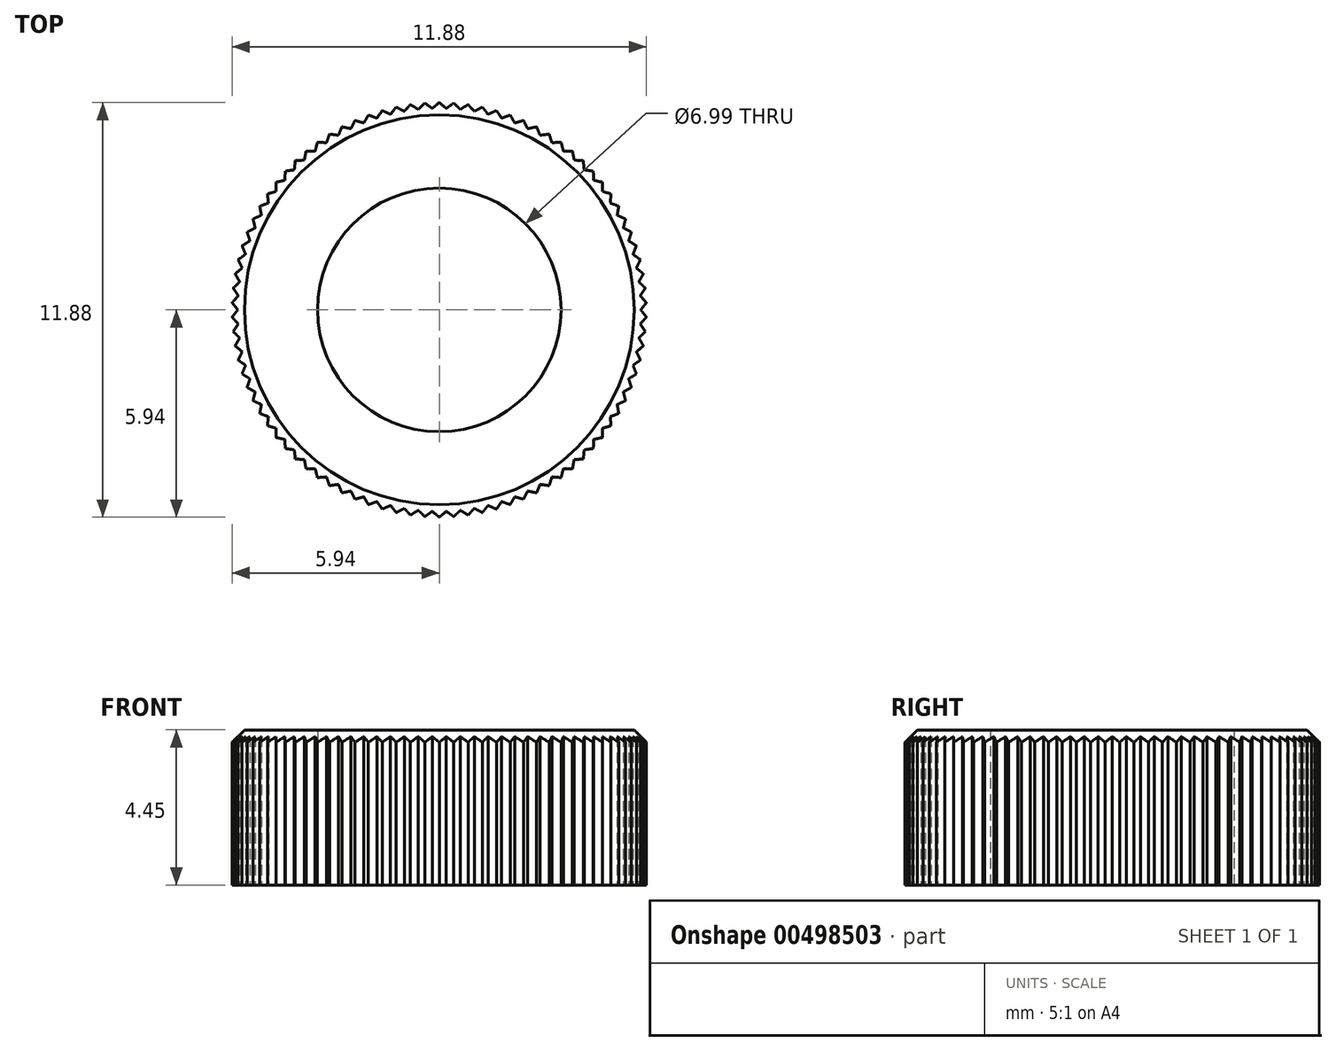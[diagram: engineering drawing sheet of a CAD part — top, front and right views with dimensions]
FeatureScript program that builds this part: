
annotation { "Feature Type Name" : "Feature", "Feature Type Description" : "" }
export const myFeature = defineFeature(function(context is Context, id is Id, definition is map)
    precondition{}
    {
        {
            var Q0;
            Q0=qCreatedBy(makeId("Front.planeOp"),FACE);
            var sketch = newSketch(context, id + "F0", { "sketchPlane" : qUnion([Q0])});
            skLineSegment(sketch, "E0", {"start": v(0, 0) * mm, "end": v(0, 10.81) * mm, "construction": true});
            skLineSegment(sketch, "E1", {"start": v(5.97, 0) * mm, "end": v(5.97, 4.45) * mm});
            skLineSegment(sketch, "E2", {"start": v(5.97, 4.45) * mm, "end": v(3.5, 4.45) * mm});
            skLineSegment(sketch, "E3", {"start": v(3.5, 4.45) * mm, "end": v(3.5, 0) * mm});
            skLineSegment(sketch, "E4", {"start": v(3.5, 0) * mm, "end": v(5.97, 0) * mm});
            skSolve(sketch);
        }
        {
            var Q0;
            Q0 = qSketchRegion(id + "F0", true);
            var Q1;
            Q1=sQuery(id+"F0.wireOp",EDGE,"E0");
            revolve(context, id + "F1", {"entities" : qUnion([Q0]), "axis" : qUnion([Q1]), "revolveType" : RevolveType.FULL});
        }
        {
            var Q0;
            Q0=makeQuery(id+"F1.opRevolve","SWEPT_EDGE",EDGE,{"disambiguationData":[OSD([sQuery(id+"F0.wireOp",EDGE,"E1"),sQuery(id+"F0.wireOp",EDGE,"E2")])]});
            chamfer(context, id + "F2", {"entities" : qUnion([Q0]), "width" : 0.38 * mm, "tangentPropagation" : true});
        }
        {
            var Q0;
            Q0=makeQuery(id+"F1.opRevolve","SWEPT_FACE",FACE,{"disambiguationData":[OSD([sQuery(id+"F0.wireOp",EDGE,"E4")])]});
            var sketch = newSketch(context, id + "F3", { "sketchPlane" : qUnion([Q0])});
            skLineSegment(sketch, "E5", {"start": v(0, 5.97) * mm, "end": v(0, 0) * mm, "construction": true});
            skPoint(sketch, "E6.orphan", {"position": v(0, 7.48) * mm});
            skCircle(sketch, "E7", {"center": v(0, 0) * mm, "radius": 5.78 * mm, "construction": true});
            skLineSegment(sketch, "E8", {"start": v(-0.2, 5.77) * mm, "end": v(0, 0) * mm, "construction": true});
            skLineSegment(sketch, "E9", {"start": v(0, 5.94) * mm, "end": v(-0.2, 5.77) * mm});
            skLineSegment(sketch, "E10.MirrorCS", {"start": v(0, 5.94) * mm, "end": v(0.2, 5.77) * mm});
            skLineSegment(sketch, "E11.1.0", {"start": v(-0.41, 5.93) * mm, "end": v(-0.2, 5.77) * mm});
            skLineSegment(sketch, "E11.1.1", {"start": v(-0.41, 5.93) * mm, "end": v(-0.6, 5.75) * mm});
            skLineSegment(sketch, "E11.2.0", {"start": v(-0.83, 5.89) * mm, "end": v(-0.6, 5.75) * mm});
            skLineSegment(sketch, "E11.2.1", {"start": v(-0.83, 5.89) * mm, "end": v(-1, 5.7) * mm});
            skLineSegment(sketch, "E11.3.0", {"start": v(-1.24, 5.81) * mm, "end": v(-1, 5.7) * mm});
            skLineSegment(sketch, "E11.3.1", {"start": v(-1.24, 5.81) * mm, "end": v(-1.4, 5.6) * mm});
            skLineSegment(sketch, "E11.4.0", {"start": v(-1.64, 5.71) * mm, "end": v(-1.4, 5.6) * mm});
            skLineSegment(sketch, "E11.4.1", {"start": v(-1.64, 5.71) * mm, "end": v(-1.79, 5.5) * mm});
            skLineSegment(sketch, "E11.5.0", {"start": v(-2.03, 5.59) * mm, "end": v(-1.79, 5.5) * mm});
            skLineSegment(sketch, "E11.5.1", {"start": v(-2.03, 5.59) * mm, "end": v(-2.16, 5.36) * mm});
            skLineSegment(sketch, "E11.6.0", {"start": v(-2.42, 5.43) * mm, "end": v(-2.16, 5.36) * mm});
            skLineSegment(sketch, "E11.6.1", {"start": v(-2.42, 5.43) * mm, "end": v(-2.53, 5.2) * mm});
            skLineSegment(sketch, "E11.7.0", {"start": v(-2.8, 5.25) * mm, "end": v(-2.53, 5.2) * mm});
            skLineSegment(sketch, "E11.7.1", {"start": v(-2.8, 5.25) * mm, "end": v(-2.89, 5) * mm});
            skLineSegment(sketch, "E11.8.0", {"start": v(-3.15, 5.04) * mm, "end": v(-2.89, 5) * mm});
            skLineSegment(sketch, "E11.8.1", {"start": v(-3.15, 5.04) * mm, "end": v(-3.23, 4.8) * mm});
            skLineSegment(sketch, "E11.9.0", {"start": v(-3.5, 4.8) * mm, "end": v(-3.23, 4.8) * mm});
            skLineSegment(sketch, "E11.9.1", {"start": v(-3.5, 4.8) * mm, "end": v(-3.56, 4.55) * mm});
            skLineSegment(sketch, "E11.10.0", {"start": v(-3.82, 4.55) * mm, "end": v(-3.56, 4.55) * mm});
            skLineSegment(sketch, "E11.10.1", {"start": v(-3.82, 4.55) * mm, "end": v(-3.87, 4.3) * mm});
            skLineSegment(sketch, "E11.11.0", {"start": v(-4.13, 4.28) * mm, "end": v(-3.87, 4.3) * mm});
            skLineSegment(sketch, "E11.11.1", {"start": v(-4.13, 4.28) * mm, "end": v(-4.16, 4.01) * mm});
            skLineSegment(sketch, "E11.12.0", {"start": v(-4.42, 3.98) * mm, "end": v(-4.16, 4.01) * mm});
            skLineSegment(sketch, "E11.12.1", {"start": v(-4.42, 3.98) * mm, "end": v(-4.43, 3.71) * mm});
            skLineSegment(sketch, "E11.13.0", {"start": v(-4.68, 3.66) * mm, "end": v(-4.43, 3.71) * mm});
            skLineSegment(sketch, "E11.13.1", {"start": v(-4.68, 3.66) * mm, "end": v(-4.67, 3.4) * mm});
            skLineSegment(sketch, "E11.14.0", {"start": v(-4.93, 3.32) * mm, "end": v(-4.67, 3.4) * mm});
            skLineSegment(sketch, "E11.14.1", {"start": v(-4.93, 3.32) * mm, "end": v(-4.9, 3.06) * mm});
            skLineSegment(sketch, "E11.15.0", {"start": v(-5.15, 2.97) * mm, "end": v(-4.9, 3.06) * mm});
            skLineSegment(sketch, "E11.15.1", {"start": v(-5.15, 2.97) * mm, "end": v(-5.1, 2.71) * mm});
            skLineSegment(sketch, "E11.16.0", {"start": v(-5.34, 2.6) * mm, "end": v(-5.1, 2.71) * mm});
            skLineSegment(sketch, "E11.16.1", {"start": v(-5.34, 2.6) * mm, "end": v(-5.28, 2.35) * mm});
            skLineSegment(sketch, "E11.17.0", {"start": v(-5.51, 2.23) * mm, "end": v(-5.28, 2.35) * mm});
            skLineSegment(sketch, "E11.17.1", {"start": v(-5.51, 2.23) * mm, "end": v(-5.43, 1.98) * mm});
            skLineSegment(sketch, "E11.18.0", {"start": v(-5.65, 1.84) * mm, "end": v(-5.43, 1.98) * mm});
            skLineSegment(sketch, "E11.18.1", {"start": v(-5.65, 1.84) * mm, "end": v(-5.55, 1.6) * mm});
            skLineSegment(sketch, "E11.19.0", {"start": v(-5.77, 1.44) * mm, "end": v(-5.55, 1.6) * mm});
            skLineSegment(sketch, "E11.19.1", {"start": v(-5.77, 1.44) * mm, "end": v(-5.65, 1.2) * mm});
            skLineSegment(sketch, "E11.20.0", {"start": v(-5.85, 1.03) * mm, "end": v(-5.65, 1.2) * mm});
            skLineSegment(sketch, "E11.20.1", {"start": v(-5.85, 1.03) * mm, "end": v(-5.72, 0.8) * mm});
            skLineSegment(sketch, "E11.21.0", {"start": v(-5.91, 0.62) * mm, "end": v(-5.72, 0.8) * mm});
            skLineSegment(sketch, "E11.21.1", {"start": v(-5.91, 0.62) * mm, "end": v(-5.76, 0.4) * mm});
            skLineSegment(sketch, "E11.22.0", {"start": v(-5.94, 0.2) * mm, "end": v(-5.76, 0.4) * mm});
            skLineSegment(sketch, "E11.22.1", {"start": v(-5.94, 0.2) * mm, "end": v(-5.78, 0) * mm});
            skLineSegment(sketch, "E11.23.0", {"start": v(-5.94, -0.2) * mm, "end": v(-5.78, 0) * mm});
            skLineSegment(sketch, "E11.23.1", {"start": v(-5.94, -0.2) * mm, "end": v(-5.76, -0.4) * mm});
            skLineSegment(sketch, "E11.24.0", {"start": v(-5.91, -0.62) * mm, "end": v(-5.76, -0.4) * mm});
            skLineSegment(sketch, "E11.24.1", {"start": v(-5.91, -0.62) * mm, "end": v(-5.72, -0.8) * mm});
            skLineSegment(sketch, "E11.25.0", {"start": v(-5.85, -1.03) * mm, "end": v(-5.72, -0.8) * mm});
            skLineSegment(sketch, "E11.25.1", {"start": v(-5.85, -1.03) * mm, "end": v(-5.65, -1.2) * mm});
            skLineSegment(sketch, "E11.26.0", {"start": v(-5.77, -1.44) * mm, "end": v(-5.65, -1.2) * mm});
            skLineSegment(sketch, "E11.26.1", {"start": v(-5.77, -1.44) * mm, "end": v(-5.55, -1.6) * mm});
            skLineSegment(sketch, "E11.27.0", {"start": v(-5.65, -1.84) * mm, "end": v(-5.55, -1.6) * mm});
            skLineSegment(sketch, "E11.27.1", {"start": v(-5.65, -1.84) * mm, "end": v(-5.43, -1.98) * mm});
            skLineSegment(sketch, "E11.28.0", {"start": v(-5.51, -2.23) * mm, "end": v(-5.43, -1.98) * mm});
            skLineSegment(sketch, "E11.28.1", {"start": v(-5.51, -2.23) * mm, "end": v(-5.28, -2.35) * mm});
            skLineSegment(sketch, "E11.29.0", {"start": v(-5.34, -2.6) * mm, "end": v(-5.28, -2.35) * mm});
            skLineSegment(sketch, "E11.29.1", {"start": v(-5.34, -2.6) * mm, "end": v(-5.1, -2.71) * mm});
            skLineSegment(sketch, "E11.30.0", {"start": v(-5.15, -2.97) * mm, "end": v(-5.1, -2.71) * mm});
            skLineSegment(sketch, "E11.30.1", {"start": v(-5.15, -2.97) * mm, "end": v(-4.9, -3.06) * mm});
            skLineSegment(sketch, "E11.31.0", {"start": v(-4.93, -3.32) * mm, "end": v(-4.9, -3.06) * mm});
            skLineSegment(sketch, "E11.31.1", {"start": v(-4.93, -3.32) * mm, "end": v(-4.67, -3.4) * mm});
            skLineSegment(sketch, "E11.32.0", {"start": v(-4.68, -3.66) * mm, "end": v(-4.67, -3.4) * mm});
            skLineSegment(sketch, "E11.32.1", {"start": v(-4.68, -3.66) * mm, "end": v(-4.43, -3.71) * mm});
            skLineSegment(sketch, "E11.33.0", {"start": v(-4.42, -3.98) * mm, "end": v(-4.43, -3.71) * mm});
            skLineSegment(sketch, "E11.33.1", {"start": v(-4.42, -3.98) * mm, "end": v(-4.16, -4.01) * mm});
            skLineSegment(sketch, "E11.34.0", {"start": v(-4.13, -4.28) * mm, "end": v(-4.16, -4.01) * mm});
            skLineSegment(sketch, "E11.34.1", {"start": v(-4.13, -4.28) * mm, "end": v(-3.87, -4.3) * mm});
            skLineSegment(sketch, "E11.35.0", {"start": v(-3.82, -4.55) * mm, "end": v(-3.87, -4.3) * mm});
            skLineSegment(sketch, "E11.35.1", {"start": v(-3.82, -4.55) * mm, "end": v(-3.56, -4.55) * mm});
            skLineSegment(sketch, "E11.36.0", {"start": v(-3.5, -4.8) * mm, "end": v(-3.56, -4.55) * mm});
            skLineSegment(sketch, "E11.36.1", {"start": v(-3.5, -4.8) * mm, "end": v(-3.23, -4.8) * mm});
            skLineSegment(sketch, "E11.37.0", {"start": v(-3.15, -5.04) * mm, "end": v(-3.23, -4.8) * mm});
            skLineSegment(sketch, "E11.37.1", {"start": v(-3.15, -5.04) * mm, "end": v(-2.89, -5) * mm});
            skLineSegment(sketch, "E11.38.0", {"start": v(-2.8, -5.25) * mm, "end": v(-2.89, -5) * mm});
            skLineSegment(sketch, "E11.38.1", {"start": v(-2.8, -5.25) * mm, "end": v(-2.53, -5.2) * mm});
            skLineSegment(sketch, "E11.39.0", {"start": v(-2.42, -5.43) * mm, "end": v(-2.53, -5.2) * mm});
            skLineSegment(sketch, "E11.39.1", {"start": v(-2.42, -5.43) * mm, "end": v(-2.16, -5.36) * mm});
            skLineSegment(sketch, "E11.40.0", {"start": v(-2.03, -5.59) * mm, "end": v(-2.16, -5.36) * mm});
            skLineSegment(sketch, "E11.40.1", {"start": v(-2.03, -5.59) * mm, "end": v(-1.79, -5.5) * mm});
            skLineSegment(sketch, "E11.41.0", {"start": v(-1.64, -5.71) * mm, "end": v(-1.79, -5.5) * mm});
            skLineSegment(sketch, "E11.41.1", {"start": v(-1.64, -5.71) * mm, "end": v(-1.4, -5.6) * mm});
            skLineSegment(sketch, "E11.42.0", {"start": v(-1.24, -5.81) * mm, "end": v(-1.4, -5.6) * mm});
            skLineSegment(sketch, "E11.42.1", {"start": v(-1.24, -5.81) * mm, "end": v(-1, -5.7) * mm});
            skLineSegment(sketch, "E11.43.0", {"start": v(-0.83, -5.89) * mm, "end": v(-1, -5.7) * mm});
            skLineSegment(sketch, "E11.43.1", {"start": v(-0.83, -5.89) * mm, "end": v(-0.6, -5.75) * mm});
            skLineSegment(sketch, "E11.44.0", {"start": v(-0.41, -5.93) * mm, "end": v(-0.6, -5.75) * mm});
            skLineSegment(sketch, "E11.44.1", {"start": v(-0.41, -5.93) * mm, "end": v(-0.2, -5.77) * mm});
            skLineSegment(sketch, "E11.45.0", {"start": v(0, -5.94) * mm, "end": v(-0.2, -5.77) * mm});
            skLineSegment(sketch, "E11.45.1", {"start": v(0, -5.94) * mm, "end": v(0.2, -5.77) * mm});
            skLineSegment(sketch, "E11.46.0", {"start": v(0.41, -5.93) * mm, "end": v(0.2, -5.77) * mm});
            skLineSegment(sketch, "E11.46.1", {"start": v(0.41, -5.93) * mm, "end": v(0.6, -5.75) * mm});
            skLineSegment(sketch, "E11.47.0", {"start": v(0.83, -5.89) * mm, "end": v(0.6, -5.75) * mm});
            skLineSegment(sketch, "E11.47.1", {"start": v(0.83, -5.89) * mm, "end": v(1, -5.7) * mm});
            skLineSegment(sketch, "E11.48.0", {"start": v(1.24, -5.81) * mm, "end": v(1, -5.7) * mm});
            skLineSegment(sketch, "E11.48.1", {"start": v(1.24, -5.81) * mm, "end": v(1.4, -5.6) * mm});
            skLineSegment(sketch, "E11.49.0", {"start": v(1.64, -5.71) * mm, "end": v(1.4, -5.6) * mm});
            skLineSegment(sketch, "E11.49.1", {"start": v(1.64, -5.71) * mm, "end": v(1.79, -5.5) * mm});
            skLineSegment(sketch, "E11.50.0", {"start": v(2.03, -5.59) * mm, "end": v(1.79, -5.5) * mm});
            skLineSegment(sketch, "E11.50.1", {"start": v(2.03, -5.59) * mm, "end": v(2.16, -5.36) * mm});
            skLineSegment(sketch, "E11.51.0", {"start": v(2.42, -5.43) * mm, "end": v(2.16, -5.36) * mm});
            skLineSegment(sketch, "E11.51.1", {"start": v(2.42, -5.43) * mm, "end": v(2.53, -5.2) * mm});
            skLineSegment(sketch, "E11.52.0", {"start": v(2.8, -5.25) * mm, "end": v(2.53, -5.2) * mm});
            skLineSegment(sketch, "E11.52.1", {"start": v(2.8, -5.25) * mm, "end": v(2.89, -5) * mm});
            skLineSegment(sketch, "E11.53.0", {"start": v(3.15, -5.04) * mm, "end": v(2.89, -5) * mm});
            skLineSegment(sketch, "E11.53.1", {"start": v(3.15, -5.04) * mm, "end": v(3.23, -4.8) * mm});
            skLineSegment(sketch, "E11.54.0", {"start": v(3.5, -4.8) * mm, "end": v(3.23, -4.8) * mm});
            skLineSegment(sketch, "E11.54.1", {"start": v(3.5, -4.8) * mm, "end": v(3.56, -4.55) * mm});
            skLineSegment(sketch, "E11.55.0", {"start": v(3.82, -4.55) * mm, "end": v(3.56, -4.55) * mm});
            skLineSegment(sketch, "E11.55.1", {"start": v(3.82, -4.55) * mm, "end": v(3.87, -4.3) * mm});
            skLineSegment(sketch, "E11.56.0", {"start": v(4.13, -4.28) * mm, "end": v(3.87, -4.3) * mm});
            skLineSegment(sketch, "E11.56.1", {"start": v(4.13, -4.28) * mm, "end": v(4.16, -4.01) * mm});
            skLineSegment(sketch, "E11.57.0", {"start": v(4.42, -3.98) * mm, "end": v(4.16, -4.01) * mm});
            skLineSegment(sketch, "E11.57.1", {"start": v(4.42, -3.98) * mm, "end": v(4.43, -3.71) * mm});
            skLineSegment(sketch, "E11.58.0", {"start": v(4.68, -3.66) * mm, "end": v(4.43, -3.71) * mm});
            skLineSegment(sketch, "E11.58.1", {"start": v(4.68, -3.66) * mm, "end": v(4.67, -3.4) * mm});
            skLineSegment(sketch, "E11.59.0", {"start": v(4.93, -3.32) * mm, "end": v(4.67, -3.4) * mm});
            skLineSegment(sketch, "E11.59.1", {"start": v(4.93, -3.32) * mm, "end": v(4.9, -3.06) * mm});
            skLineSegment(sketch, "E11.60.0", {"start": v(5.15, -2.97) * mm, "end": v(4.9, -3.06) * mm});
            skLineSegment(sketch, "E11.60.1", {"start": v(5.15, -2.97) * mm, "end": v(5.1, -2.71) * mm});
            skLineSegment(sketch, "E11.61.0", {"start": v(5.34, -2.6) * mm, "end": v(5.1, -2.71) * mm});
            skLineSegment(sketch, "E11.61.1", {"start": v(5.34, -2.6) * mm, "end": v(5.28, -2.35) * mm});
            skLineSegment(sketch, "E11.62.0", {"start": v(5.51, -2.23) * mm, "end": v(5.28, -2.35) * mm});
            skLineSegment(sketch, "E11.62.1", {"start": v(5.51, -2.23) * mm, "end": v(5.43, -1.98) * mm});
            skLineSegment(sketch, "E11.63.0", {"start": v(5.65, -1.84) * mm, "end": v(5.43, -1.98) * mm});
            skLineSegment(sketch, "E11.63.1", {"start": v(5.65, -1.84) * mm, "end": v(5.55, -1.6) * mm});
            skLineSegment(sketch, "E11.64.0", {"start": v(5.77, -1.44) * mm, "end": v(5.55, -1.6) * mm});
            skLineSegment(sketch, "E11.64.1", {"start": v(5.77, -1.44) * mm, "end": v(5.65, -1.2) * mm});
            skLineSegment(sketch, "E11.65.0", {"start": v(5.85, -1.03) * mm, "end": v(5.65, -1.2) * mm});
            skLineSegment(sketch, "E11.65.1", {"start": v(5.85, -1.03) * mm, "end": v(5.72, -0.8) * mm});
            skLineSegment(sketch, "E11.66.0", {"start": v(5.91, -0.62) * mm, "end": v(5.72, -0.8) * mm});
            skLineSegment(sketch, "E11.66.1", {"start": v(5.91, -0.62) * mm, "end": v(5.76, -0.4) * mm});
            skLineSegment(sketch, "E11.67.0", {"start": v(5.94, -0.2) * mm, "end": v(5.76, -0.4) * mm});
            skLineSegment(sketch, "E11.67.1", {"start": v(5.94, -0.2) * mm, "end": v(5.78, 0) * mm});
            skLineSegment(sketch, "E11.68.0", {"start": v(5.94, 0.2) * mm, "end": v(5.78, 0) * mm});
            skLineSegment(sketch, "E11.68.1", {"start": v(5.94, 0.2) * mm, "end": v(5.76, 0.4) * mm});
            skLineSegment(sketch, "E11.69.0", {"start": v(5.91, 0.62) * mm, "end": v(5.76, 0.4) * mm});
            skLineSegment(sketch, "E11.69.1", {"start": v(5.91, 0.62) * mm, "end": v(5.72, 0.8) * mm});
            skLineSegment(sketch, "E11.70.0", {"start": v(5.85, 1.03) * mm, "end": v(5.72, 0.8) * mm});
            skLineSegment(sketch, "E11.70.1", {"start": v(5.85, 1.03) * mm, "end": v(5.65, 1.2) * mm});
            skLineSegment(sketch, "E11.71.0", {"start": v(5.77, 1.44) * mm, "end": v(5.65, 1.2) * mm});
            skLineSegment(sketch, "E11.71.1", {"start": v(5.77, 1.44) * mm, "end": v(5.55, 1.6) * mm});
            skLineSegment(sketch, "E11.72.0", {"start": v(5.65, 1.84) * mm, "end": v(5.55, 1.6) * mm});
            skLineSegment(sketch, "E11.72.1", {"start": v(5.65, 1.84) * mm, "end": v(5.43, 1.98) * mm});
            skLineSegment(sketch, "E11.73.0", {"start": v(5.51, 2.23) * mm, "end": v(5.43, 1.98) * mm});
            skLineSegment(sketch, "E11.73.1", {"start": v(5.51, 2.23) * mm, "end": v(5.28, 2.35) * mm});
            skLineSegment(sketch, "E11.74.0", {"start": v(5.34, 2.6) * mm, "end": v(5.28, 2.35) * mm});
            skLineSegment(sketch, "E11.74.1", {"start": v(5.34, 2.6) * mm, "end": v(5.1, 2.71) * mm});
            skLineSegment(sketch, "E11.75.0", {"start": v(5.15, 2.97) * mm, "end": v(5.1, 2.71) * mm});
            skLineSegment(sketch, "E11.75.1", {"start": v(5.15, 2.97) * mm, "end": v(4.9, 3.06) * mm});
            skLineSegment(sketch, "E11.76.0", {"start": v(4.93, 3.32) * mm, "end": v(4.9, 3.06) * mm});
            skLineSegment(sketch, "E11.76.1", {"start": v(4.93, 3.32) * mm, "end": v(4.67, 3.4) * mm});
            skLineSegment(sketch, "E11.77.0", {"start": v(4.68, 3.66) * mm, "end": v(4.67, 3.4) * mm});
            skLineSegment(sketch, "E11.77.1", {"start": v(4.68, 3.66) * mm, "end": v(4.43, 3.71) * mm});
            skLineSegment(sketch, "E11.78.0", {"start": v(4.42, 3.98) * mm, "end": v(4.43, 3.71) * mm});
            skLineSegment(sketch, "E11.78.1", {"start": v(4.42, 3.98) * mm, "end": v(4.16, 4.01) * mm});
            skLineSegment(sketch, "E11.79.0", {"start": v(4.13, 4.28) * mm, "end": v(4.16, 4.01) * mm});
            skLineSegment(sketch, "E11.79.1", {"start": v(4.13, 4.28) * mm, "end": v(3.87, 4.3) * mm});
            skLineSegment(sketch, "E11.80.0", {"start": v(3.82, 4.55) * mm, "end": v(3.87, 4.3) * mm});
            skLineSegment(sketch, "E11.80.1", {"start": v(3.82, 4.55) * mm, "end": v(3.56, 4.55) * mm});
            skLineSegment(sketch, "E11.81.0", {"start": v(3.5, 4.8) * mm, "end": v(3.56, 4.55) * mm});
            skLineSegment(sketch, "E11.81.1", {"start": v(3.5, 4.8) * mm, "end": v(3.23, 4.8) * mm});
            skLineSegment(sketch, "E11.82.0", {"start": v(3.15, 5.04) * mm, "end": v(3.23, 4.8) * mm});
            skLineSegment(sketch, "E11.82.1", {"start": v(3.15, 5.04) * mm, "end": v(2.89, 5) * mm});
            skLineSegment(sketch, "E11.83.0", {"start": v(2.8, 5.25) * mm, "end": v(2.89, 5) * mm});
            skLineSegment(sketch, "E11.83.1", {"start": v(2.8, 5.25) * mm, "end": v(2.53, 5.2) * mm});
            skLineSegment(sketch, "E11.84.0", {"start": v(2.42, 5.43) * mm, "end": v(2.53, 5.2) * mm});
            skLineSegment(sketch, "E11.84.1", {"start": v(2.42, 5.43) * mm, "end": v(2.16, 5.36) * mm});
            skLineSegment(sketch, "E11.85.0", {"start": v(2.03, 5.59) * mm, "end": v(2.16, 5.36) * mm});
            skLineSegment(sketch, "E11.85.1", {"start": v(2.03, 5.59) * mm, "end": v(1.79, 5.5) * mm});
            skLineSegment(sketch, "E11.86.0", {"start": v(1.64, 5.71) * mm, "end": v(1.79, 5.5) * mm});
            skLineSegment(sketch, "E11.86.1", {"start": v(1.64, 5.71) * mm, "end": v(1.4, 5.6) * mm});
            skLineSegment(sketch, "E11.87.0", {"start": v(1.24, 5.81) * mm, "end": v(1.4, 5.6) * mm});
            skLineSegment(sketch, "E11.87.1", {"start": v(1.24, 5.81) * mm, "end": v(1, 5.7) * mm});
            skLineSegment(sketch, "E11.88.0", {"start": v(0.83, 5.89) * mm, "end": v(1, 5.7) * mm});
            skLineSegment(sketch, "E11.88.1", {"start": v(0.83, 5.89) * mm, "end": v(0.6, 5.75) * mm});
            skLineSegment(sketch, "E11.89.0", {"start": v(0.41, 5.93) * mm, "end": v(0.6, 5.75) * mm});
            skLineSegment(sketch, "E11.89.1", {"start": v(0.41, 5.93) * mm, "end": v(0.2, 5.77) * mm});
            skCircle(sketch, "E12", {"center": v(0, 0) * mm, "radius": 6.35 * mm});
            skSolve(sketch);
        }
        {
            var Q0;
            Q0 = qSketchRegion(id + "F3", true);
            extrude(context, id + "F4", {"entities" : qUnion([Q0]), "operationType" : NewBodyOperationType.REMOVE, "endBound" : BoundingType.THROUGH_ALL, "oppositeDirection" : true, "depth" : 25.4 * mm});
        }
    });
